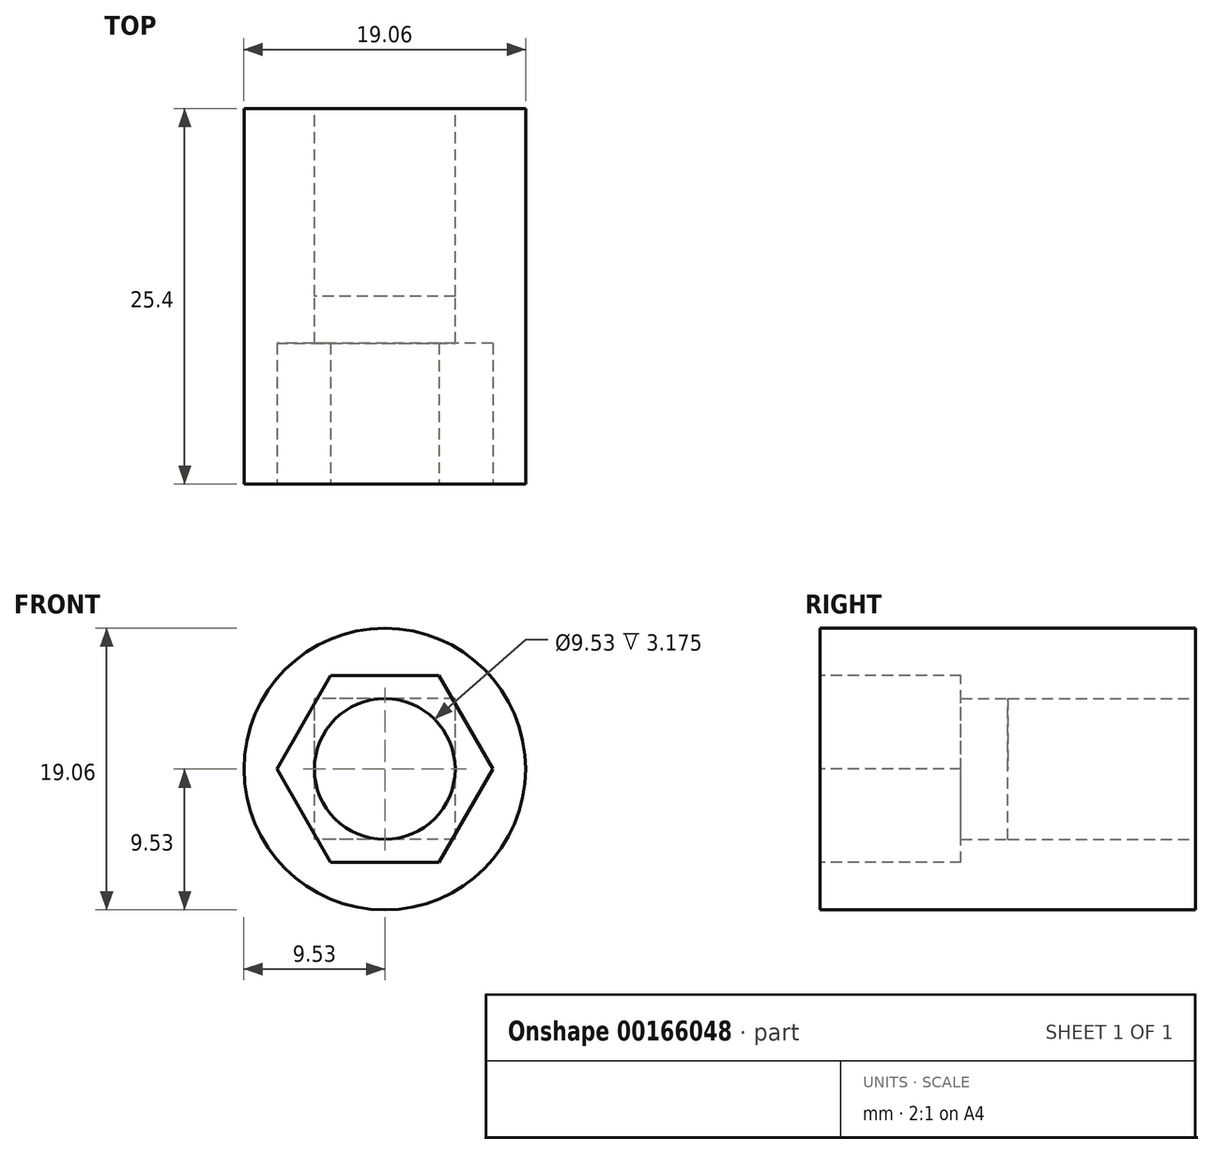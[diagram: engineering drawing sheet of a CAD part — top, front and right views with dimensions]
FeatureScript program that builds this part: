
annotation { "Feature Type Name" : "Feature", "Feature Type Description" : "" }
export const myFeature = defineFeature(function(context is Context, id is Id, definition is map)
    precondition{}
    {
        {
            var Q0;
            Q0=qCreatedBy(makeId("Front.planeOp"),FACE);
            var sketch = newSketch(context, id + "F0", { "sketchPlane" : qUnion([Q0])});
            skCircle(sketch, "E0", {"center": v(0, 0) * mm, "radius": 9.53 * mm});
            skSolve(sketch);
        }
        {
            var Q0;
            Q0 = qSketchRegion(id + "F0", true);
            extrude(context, id + "F1", {"entities" : qUnion([Q0]), "depth" : 25.4 * mm});
        }
        {
            var Q0;
            Q0=makeQuery(id+"F1.opExtrude","CAP_FACE",FACE,{"disambiguationData":[OSD([sQuery(id+"F0.wireOp",EDGE,"E0")])],"isStart":true});
            var sketch = newSketch(context, id + "F2", { "sketchPlane" : qUnion([Q0])});
            skLineSegment(sketch, "E1.bottom", {"start": v(-4.76, -4.76) * mm, "end": v(4.76, -4.76) * mm});
            skLineSegment(sketch, "E1.top", {"start": v(-4.76, 4.76) * mm, "end": v(4.76, 4.76) * mm});
            skLineSegment(sketch, "E1.left", {"start": v(-4.76, -4.76) * mm, "end": v(-4.76, 4.76) * mm});
            skLineSegment(sketch, "E1.right", {"start": v(4.76, -4.76) * mm, "end": v(4.76, 4.76) * mm});
            skPoint(sketch, "E1.middle", {"position": v(0, 0) * mm});
            skCircle(sketch, "E2", {"center": v(0, 0) * mm, "radius": 4.76 * mm});
            skSolve(sketch);
        }
        {
            var Q0;
            {var subQ0=sQuery(id+"F2.wireOp",EDGE,"E2");var subQ1=makeQuery(id+"F2.imprint","INTERSECT",VERTEX,{"derivedFrom":[sQuery(id+"F2.wireOp",EDGE,"E1.top"),subQ0]});Q0=makeQuery(id+"F2.imprint","IMPRINT",FACE,{"disambiguationData":[TD([[makeQuery(id+"F2.imprint","IMPRINT",EDGE,{"disambiguationData":[TD([[subQ1,1.0]])],"derivedFrom":subQ0}),1.0]])]});}
            extrude(context, id + "F3", {"entities" : qUnion([Q0]), "operationType" : NewBodyOperationType.REMOVE, "endBound" : BoundingType.THROUGH_ALL, "oppositeDirection" : true, "depth" : 25.4 * mm});
        }
        {
            var Q0;
            Q0 = qSketchRegion(id + "F2", true);
            extrude(context, id + "F4", {"entities" : qUnion([Q0]), "operationType" : NewBodyOperationType.REMOVE, "oppositeDirection" : true, "depth" : 12.7 * mm});
        }
        {
            var Q0;
            Q0=makeQuery(id+"F1.opExtrude","CAP_FACE",FACE,{"disambiguationData":[OSD([sQuery(id+"F0.wireOp",EDGE,"E0")])],"isStart":false});
            var sketch = newSketch(context, id + "F5", { "sketchPlane" : qUnion([Q0])});
            skCircle(sketch, "E3.cCircle", {"center": v(0, 0) * mm, "radius": 6.32 * mm, "construction": true});
            skLineSegment(sketch, "E3.0", {"start": v(-3.65, 6.32) * mm, "end": v(3.65, 6.32) * mm});
            skLineSegment(sketch, "E3.1", {"start": v(3.65, 6.32) * mm, "end": v(7.3, 0) * mm});
            skLineSegment(sketch, "E3.2", {"start": v(7.3, 0) * mm, "end": v(3.65, -6.32) * mm});
            skLineSegment(sketch, "E3.3", {"start": v(3.65, -6.32) * mm, "end": v(-3.65, -6.32) * mm});
            skLineSegment(sketch, "E3.4", {"start": v(-3.65, -6.32) * mm, "end": v(-7.3, 0) * mm});
            skLineSegment(sketch, "E3.5", {"start": v(-7.3, 0) * mm, "end": v(-3.65, 6.32) * mm});
            skPoint(sketch, "E3.0.midPoint", {"position": v(0, 6.32) * mm});
            skSolve(sketch);
        }
        {
            var Q0;
            Q0=makeQuery(id+"F5.imprint","IMPRINT",FACE,{"disambiguationData":[TD([[makeQuery(id+"F5.imprint","IMPRINT",EDGE,{"derivedFrom":sQuery(id+"F5.wireOp",EDGE,"E3.0")}),-1.0]])]});
            extrude(context, id + "F6", {"entities" : qUnion([Q0]), "operationType" : NewBodyOperationType.REMOVE, "oppositeDirection" : true, "depth" : 9.52 * mm});
        }
    });
